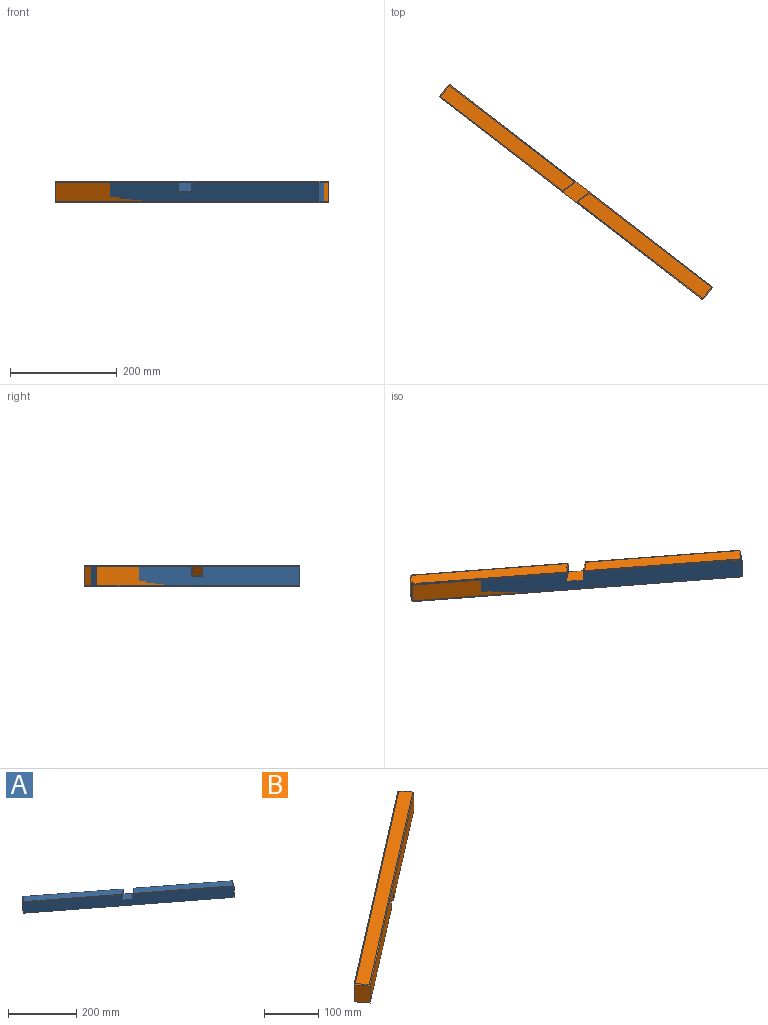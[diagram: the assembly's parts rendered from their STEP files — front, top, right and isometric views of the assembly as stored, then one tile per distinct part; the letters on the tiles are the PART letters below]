
ASSEMBLY  parts=2 mates=1
PART A: 18 faces, bbox 512.9x404.2x40 mm
  f0: plane 24.6x18.92mm, normal (0.61,-0.79,0), area 558.7mm2, adj f1,f3,f9,f10
  f1: plane 494.6x380.46mm, normal (0.61,0.79,0), area 23153.3mm2, adj f0,f2,f5,f6,f7,f9,f11,f14
  f2: plane 38x23.78mm, normal (-0.79,0.61,0), area 1140mm2, adj f1,f3,f5,f13
  f3: plane 494.6x380.46mm, normal (-0.61,-0.79,0), area 23153.3mm2, adj f0,f2,f5,f6,f7,f9,f12,f17
  f4: plane 250.36x196.79mm, normal (0,0,1), area 7602.7mm2, adj f10,f11,f12,f13
  f5: plane 512.89x404.24mm, normal (0,0,-1), area 18720mm2, adj f1,f2,f3,f7
  f6: plane 24.6x18.92mm, normal (-0.61,0.79,0), area 558.7mm2, adj f1,f3,f9,f15
  f7: plane 38x23.78mm, normal (0.79,-0.61,0), area 1140mm2, adj f1,f3,f5,f16
  f8: plane 250.36x196.79mm, normal (0,0,1), area 7602.7mm2, adj f14,f15,f16,f17
  f9: plane 49.2x37.85mm, normal (0,0,1), area 931.2mm2, adj f0,f1,f3,f6
  f10: plane 24.6x18.92mm, normal (0.43,-0.56,0.71), area 81.9mm2, adj f0,f4,f11,f12
  f11: plane 238.15x183.19mm, normal (0.43,0.56,0.71), area 843.3mm2, adj f1,f4,f10,f13
  f12: plane 231.84x178.71mm, normal (-0.43,-0.56,0.71), area 822.3mm2, adj f3,f4,f10,f13
  f13: plane 23.78x18.66mm, normal (-0.56,0.43,0.71), area 79.2mm2, adj f2,f4,f11,f12
  f14: plane 231.84x178.71mm, normal (0.43,0.56,0.71), area 822.3mm2, adj f1,f8,f15,f16
  f15: plane 24.6x18.92mm, normal (-0.43,0.56,0.71), area 81.9mm2, adj f6,f8,f14,f17
  f16: plane 23.78x18.66mm, normal (0.56,-0.43,0.71), area 79.2mm2, adj f7,f8,f14,f17
  f17: plane 238.15x183.19mm, normal (-0.43,-0.56,0.71), area 843.3mm2, adj f3,f8,f15,f16
PART B: 14 faces, bbox 512.9x404.2x40 mm
  f0: plane 24.6x20mm, normal (-0.61,-0.79,0), area 620.8mm2, adj f1,f3,f4,f9
  f1: plane 494.6x380.46mm, normal (0.61,-0.79,0), area 23091.2mm2, adj f0,f2,f4,f6,f7,f8,f9,f13
  f2: plane 38x23.78mm, normal (0.79,0.61,0), area 1140mm2, adj f1,f3,f4,f12
  f3: plane 494.6x380.46mm, normal (-0.61,0.79,0), area 23091.2mm2, adj f0,f2,f4,f6,f7,f8,f9,f10
  f4: plane 256.44x202.12mm, normal (0,0,-1), area 8894.4mm2, adj f0,f1,f2,f3
  f5: plane 507.28x398.63mm, normal (0,0,1), area 16120mm2, adj f10,f11,f12,f13
  f6: plane 24.6x20mm, normal (0.61,0.79,0), area 620.8mm2, adj f1,f3,f8,f9
  f7: plane 38x23.78mm, normal (-0.79,-0.61,0), area 1140mm2, adj f1,f3,f8,f11
  f8: plane 256.44x202.12mm, normal (0,0,-1), area 8894.4mm2, adj f1,f3,f6,f7
  f9: plane 49.2x37.85mm, normal (0,0,-1), area 931.2mm2, adj f0,f1,f3,f6
  f10: plane 494.6x380.83mm, normal (-0.43,0.56,0.71), area 1759.3mm2, adj f3,f5,f11,f12
  f11: plane 23.78x18.66mm, normal (-0.56,-0.43,0.71), area 79.2mm2, adj f5,f7,f10,f13
  f12: plane 23.78x18.66mm, normal (0.56,0.43,0.71), area 79.2mm2, adj f2,f5,f10,f13
  f13: plane 494.6x380.83mm, normal (0.43,-0.56,0.71), area 1759.3mm2, adj f1,f5,f11,f12
PLACE A t=(837.14,-196.86,-258.48)mm
PLACE B rot(axis=(1,0,0),180deg) t=(-722.86,265.95,-258.48)mm
MATE fastened B.f7 <-> A.f2  axis (-0.79,0.61,0) through (87.91,224.77,-238.48)mm
